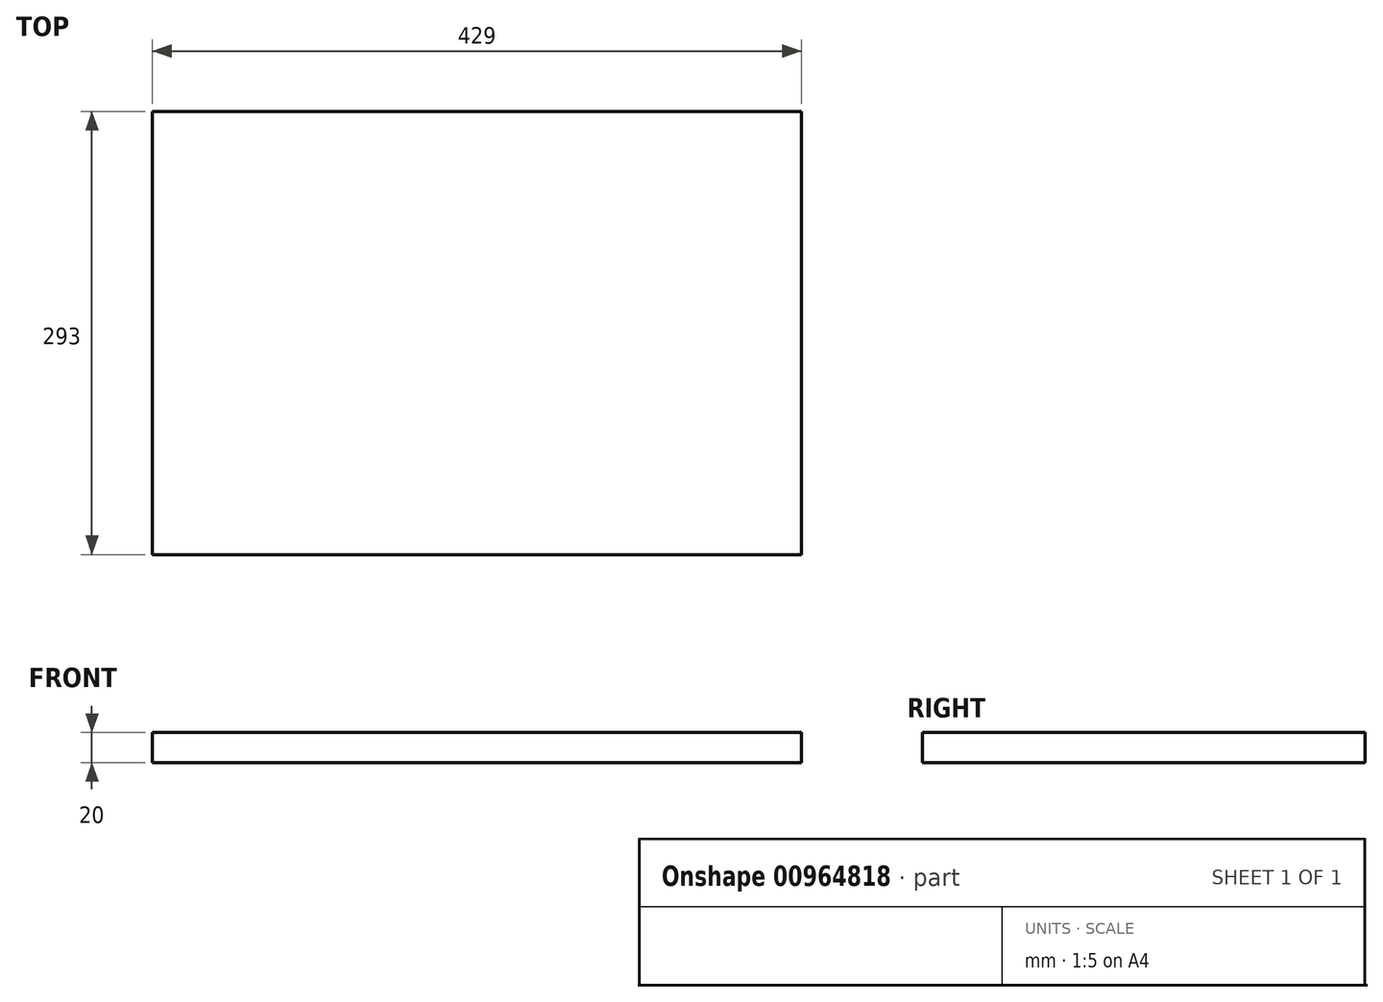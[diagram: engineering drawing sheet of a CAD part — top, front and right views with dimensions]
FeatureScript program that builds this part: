
annotation { "Feature Type Name" : "Feature", "Feature Type Description" : "" }
export const myFeature = defineFeature(function(context is Context, id is Id, definition is map)
    precondition{}
    {
        {
            var Q0;
            Q0=qCreatedBy(makeId("Top.planeOp"),FACE);
            var sketch = newSketch(context, id + "F0", { "sketchPlane" : qUnion([Q0])});
            skLineSegment(sketch, "E0.bottom", {"start": v(-384.84, 266.97) * mm, "end": v(44.16, 266.97) * mm});
            skLineSegment(sketch, "E0.top", {"start": v(-384.84, -26.03) * mm, "end": v(44.16, -26.03) * mm});
            skLineSegment(sketch, "E0.left", {"start": v(-384.84, 266.97) * mm, "end": v(-384.84, -26.03) * mm});
            skLineSegment(sketch, "E0.right", {"start": v(44.16, 266.97) * mm, "end": v(44.16, -26.03) * mm});
            skSolve(sketch);
        }
        {
            var Q0;
            Q0 = qSketchRegion(id + "F0", true);
            extrude(context, id + "F1", {"entities" : qUnion([Q0]), "depth" : 20 * mm, "offsetDistance" : 25 * mm});
        }
    });
